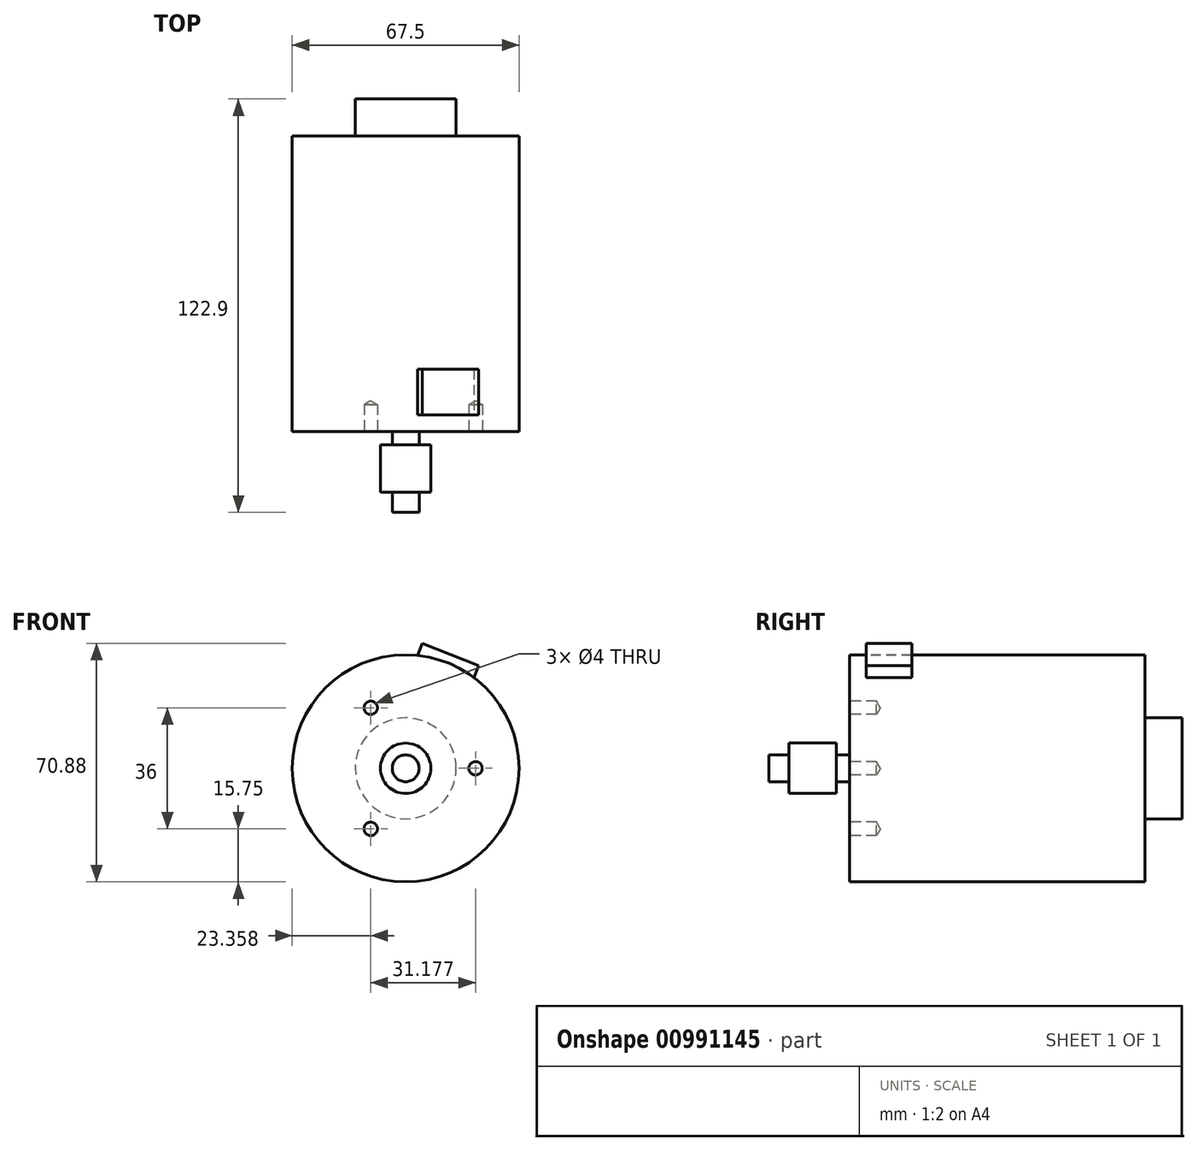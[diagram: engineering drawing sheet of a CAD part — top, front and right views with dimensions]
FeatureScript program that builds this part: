
annotation { "Feature Type Name" : "Feature", "Feature Type Description" : "" }
export const myFeature = defineFeature(function(context is Context, id is Id, definition is map)
    precondition{}
    {
        {
            var Q0;
            Q0=qCreatedBy(makeId("Front.planeOp"),FACE);
            var sketch = newSketch(context, id + "F0", { "sketchPlane" : qUnion([Q0])});
            skCircle(sketch, "E0", {"center": v(0, 0) * mm, "radius": 33.75 * mm});
            skPoint(sketch, "E1", {"position": v(20.78, 0) * mm});
            skPoint(sketch, "E2.1.0", {"position": v(-10.4, 18) * mm});
            skPoint(sketch, "E2.2.0", {"position": v(-10.4, -18) * mm});
            skSolve(sketch);
        }
        {
            var Q0;
            Q0=makeQuery(id+"F0.imprint","IMPRINT",FACE,{"disambiguationData":[TD([[makeQuery(id+"F0.imprint","IMPRINT",EDGE,{"derivedFrom":sQuery(id+"F0.wireOp",EDGE,"E0")}),1.0]])]});
            extrude(context, id + "F1", {"entities" : qUnion([Q0]), "oppositeDirection" : true, "depth" : 87.9 * mm, "offsetDistance" : 25 * mm});
        }
        {
            var Q0;
            Q0=makeQuery(id+"F1.opExtrude","CAP_FACE",FACE,{"disambiguationData":[OSD([sQuery(id+"F0.wireOp",EDGE,"E0")])],"isStart":false});
            var sketch = newSketch(context, id + "F2", { "sketchPlane" : qUnion([Q0])});
            skCircle(sketch, "E3", {"center": v(0, 0) * mm, "radius": 15 * mm});
            skSolve(sketch);
        }
        {
            var Q0;
            Q0 = qSketchRegion(id + "F2", true);
            extrude(context, id + "F3", {"entities" : qUnion([Q0]), "operationType" : NewBodyOperationType.ADD, "depth" : 11 * mm, "offsetDistance" : 25 * mm});
        }
        {
            var Q0;
            Q0=makeQuery(id+"F1.opExtrude","CAP_FACE",FACE,{"disambiguationData":[OSD([sQuery(id+"F0.wireOp",EDGE,"E0")])],"isStart":true});
            var sketch = newSketch(context, id + "F4", { "sketchPlane" : qUnion([Q0])});
            skCircle(sketch, "E4", {"center": v(0, 0) * mm, "radius": 4 * mm});
            skSolve(sketch);
        }
        {
            var Q0;
            Q0 = qSketchRegion(id + "F4", true);
            extrude(context, id + "F5", {"entities" : qUnion([Q0]), "operationType" : NewBodyOperationType.ADD, "depth" : 24 * mm, "offsetDistance" : 25 * mm});
        }
        {
            var Q0;
            Q0=sQuery(id+"F0.wireOp",VERTEX,"E1");
            var Q1;
            Q1=sQuery(id+"F0.wireOp",VERTEX,"E2.1.0");
            var Q2;
            Q2=sQuery(id+"F0.wireOp",VERTEX,"E2.2.0");
            var Q3;
            Q3=makeQuery(id+"F1.opExtrude","SWEPT_BODY",BODY,{"disambiguationData":[OSD([sQuery(id+"F0.wireOp",EDGE,"E0")])]});
            hole(context, id + "F6", {"style" : HoleStyle.SIMPLE, "endStyle" : HoleEndStyle.BLIND, "holeDiameter" : 4 * mm, "majorDiameter" : 5 * mm, "holeDepth" : 8 * mm, "isTappedThrough" : true, "tappedDepth" : 12 * mm, "tapClearance" : 3, "locations" : qUnion([Q0, Q1, Q2]), "scope" : qUnion([Q3])});
        }
        {
            var Q0;
            Q0=makeQuery(id+"F0.imprint","IMPRINT",FACE,{"disambiguationData":[TD([[makeQuery(id+"F0.imprint","IMPRINT",EDGE,{"derivedFrom":sQuery(id+"F0.wireOp",EDGE,"E0")}),1.0]])]});
            cPlane(context, id + "F7", {"entities" : qUnion([Q0]), "cplaneType" : CPlaneType.OFFSET, "offset" : 4 * mm, "width" : 150 * mm, "height" : 150 * mm});
        }
        {
            var Q0;
            Q0=qCreatedBy(id+"F7.planeOp",FACE);
            var sketch = newSketch(context, id + "F8", { "sketchPlane" : qUnion([Q0])});
            skCircle(sketch, "E5", {"center": v(0, 0) * mm, "radius": 7.5 * mm});
            skSolve(sketch);
        }
        {
            var Q0;
            Q0 = qSketchRegion(id + "F8", true);
            extrude(context, id + "F9", {"entities" : qUnion([Q0]), "operationType" : NewBodyOperationType.ADD, "depth" : 14 * mm, "offsetDistance" : 25 * mm});
        }
        {
            var Q0;
            Q0=qCreatedBy(id+"F7.planeOp",FACE);
            cPlane(context, id + "F10", {"entities" : qUnion([Q0]), "cplaneType" : CPlaneType.OFFSET, "offset" : 9 * mm, "oppositeDirection" : true, "width" : 150 * mm, "height" : 150 * mm});
        }
        {
            var Q0;
            Q0=qCreatedBy(id+"F10.planeOp",FACE);
            var sketch = newSketch(context, id + "F11", { "sketchPlane" : qUnion([Q0])});
            skLineSegment(sketch, "E6", {"start": v(21.66, 30.55) * mm, "end": v(4.9, 37.13) * mm});
            skLineSegment(sketch, "E7", {"start": v(0, 0) * mm, "end": v(13.28, 33.84) * mm, "construction": true});
            skPoint(sketch, "E7.endSnap0", {"position": v(13.28, 33.84) * mm});
            skCircle(sketch, "E8.0", {"center": v(0, 0) * mm, "radius": 33.75 * mm, "construction": true});
            skLineSegment(sketch, "E9", {"start": v(21.66, 30.55) * mm, "end": v(20.26, 27) * mm});
            skLineSegment(sketch, "E10", {"start": v(4.9, 37.13) * mm, "end": v(3.5, 33.57) * mm});
            skArc(sketch, "E11", {"start": v(20.26, 27) * mm, "mid": v(12.33, 31.42) * mm, "end": v(3.5, 33.57) * mm});
            skLineSegment(sketch, "E12", {"start": v(0, 0) * mm, "end": v(-38.8, 0) * mm, "construction": true});
            skPoint(sketch, "E13.0", {"position": v(-10.4, 18) * mm});
            skLineSegment(sketch, "E14", {"start": v(0, 0) * mm, "end": v(-10.4, 18) * mm, "construction": true});
            skLineSegment(sketch, "E15", {"start": v(-10.4, 18) * mm, "end": v(4.73, 12.06) * mm, "construction": true});
            skSolve(sketch);
        }
        {
            var Q0;
            Q0 = qSketchRegion(id + "F11", true);
            extrude(context, id + "F12", {"entities" : qUnion([Q0]), "operationType" : NewBodyOperationType.ADD, "oppositeDirection" : true, "depth" : 13.5 * mm, "offsetDistance" : 25 * mm});
        }
    });
